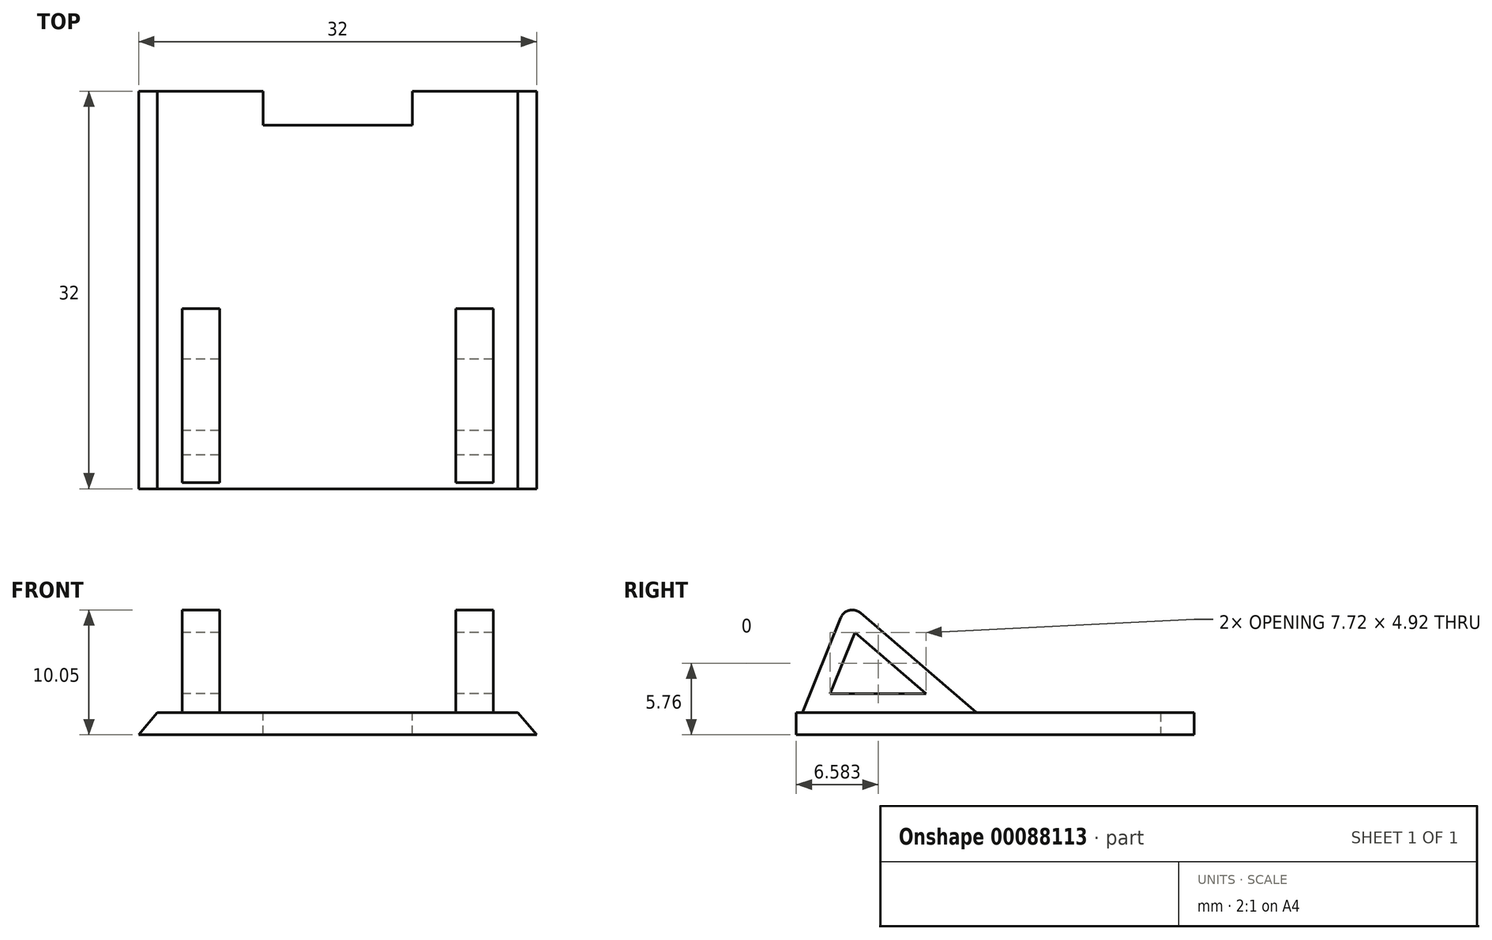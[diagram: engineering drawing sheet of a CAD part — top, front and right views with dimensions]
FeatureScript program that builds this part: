
annotation { "Feature Type Name" : "Feature", "Feature Type Description" : "" }
export const myFeature = defineFeature(function(context is Context, id is Id, definition is map)
    precondition{}
    {
        {
            var Q0;
            Q0=qCreatedBy(makeId("Front.planeOp"),FACE);
            var sketch = newSketch(context, id + "F2", { "sketchPlane" : qUnion([Q0])});
            skLineSegment(sketch, "E0", {"start": v(0, 0) * mm, "end": v(16, 0) * mm});
            skLineSegment(sketch, "E1", {"start": v(0, 0) * mm, "end": v(0, 1.8) * mm});
            skLineSegment(sketch, "E2", {"start": v(0, 1.8) * mm, "end": v(0, 1.8) * mm});
            skLineSegment(sketch, "E3", {"start": v(0, 1.8) * mm, "end": v(14.5, 1.8) * mm});
            skLineSegment(sketch, "E4", {"start": v(16, 0) * mm, "end": v(14.5, 1.8) * mm});
            skLineSegment(sketch, "E5.MirrorCS", {"start": v(0, 1.8) * mm, "end": v(-14.5, 1.8) * mm});
            skLineSegment(sketch, "E6.MirrorCS", {"start": v(0, 0) * mm, "end": v(-16, 0) * mm});
            skLineSegment(sketch, "E7.MirrorCS", {"start": v(-16, 0) * mm, "end": v(-14.5, 1.8) * mm});
            skSolve(sketch);
        }
        {
            var Q0;
            Q0 = qSketchRegion(id + "F2", true);
            extrude(context, id + "F3", {"entities" : qUnion([Q0]), "endBound" : BoundingType.SYMMETRIC, "depth" : 32 * mm});
        }
        {
            var Q0;
            Q0=qCreatedBy(makeId("Top.planeOp"),FACE);
            var sketch = newSketch(context, id + "F4", { "sketchPlane" : qUnion([Q0])});
            skLineSegment(sketch, "E8", {"start": v(0, 0) * mm, "end": v(0, 14.7) * mm, "construction": true});
            skLineSegment(sketch, "E9.bottom", {"start": v(-6, 16.12) * mm, "end": v(6, 16.12) * mm});
            skLineSegment(sketch, "E9.top", {"start": v(-6, 13.28) * mm, "end": v(6, 13.28) * mm});
            skLineSegment(sketch, "E9.left", {"start": v(-6, 16.12) * mm, "end": v(-6, 13.28) * mm});
            skLineSegment(sketch, "E9.right", {"start": v(6, 16.12) * mm, "end": v(6, 13.28) * mm});
            skPoint(sketch, "E9.middle", {"position": v(0, 14.7) * mm});
            skSolve(sketch);
        }
        {
            var Q0;
            Q0 = qSketchRegion(id + "F4", true);
            extrude(context, id + "F5", {"entities" : qUnion([Q0]), "operationType" : NewBodyOperationType.REMOVE, "depth" : 25 * mm});
        }
        {
            var Q0;
            Q0=qCreatedBy(makeId("Right.planeOp"),FACE);
            var sketch = newSketch(context, id + "F0", { "sketchPlane" : qUnion([Q0])});
            skLineSegment(sketch, "E10", {"start": v(0, 0) * mm, "end": v(-15.5, 0) * mm, "construction": true});
            skLineSegment(sketch, "E11", {"start": v(-15.5, 0) * mm, "end": v(-15.5, 1.8) * mm, "construction": true});
            skLineSegment(sketch, "E12", {"start": v(-15.5, 1.8) * mm, "end": v(-15.5, 11.63) * mm});
            skLineSegment(sketch, "E13", {"start": v(-10.85, 9.81) * mm, "end": v(-1.5, 1.8) * mm});
            skLineSegment(sketch, "E14", {"start": v(-1.5, 1.8) * mm, "end": v(-15.5, 1.8) * mm});
            skLineSegment(sketch, "E15", {"start": v(-15.5, 1.8) * mm, "end": v(-12.43, 9.43) * mm});
            skPoint(sketch, "E16.visualSharp", {"position": v(-15.5, 13.8) * mm});
            skArc(sketch, "E16.filletArc", {"start": v(-13.85, 12.39) * mm, "mid": v(-14.92, 12.53) * mm, "end": v(-15.5, 11.63) * mm});
            skArc(sketch, "E17.filletArc", {"start": v(-10.85, 9.81) * mm, "mid": v(-11.74, 10.02) * mm, "end": v(-12.43, 9.43) * mm});
            skLineSegment(sketch, "E18", {"start": v(-13.85, 12.39) * mm, "end": v(-10.85, 9.81) * mm});
            skLineSegment(sketch, "E19.0", {"start": v(-11.3, 8.22) * mm, "end": v(-5.55, 3.3) * mm});
            skLineSegment(sketch, "E19.1", {"start": v(-13.28, 3.3) * mm, "end": v(-11.3, 8.22) * mm});
            skLineSegment(sketch, "E19.2", {"start": v(-5.55, 3.3) * mm, "end": v(-13.28, 3.3) * mm});
            skSolve(sketch);
        }
        {
            var Q0;
            {var subQ0=sQuery(id+"F0.wireOp",EDGE,"E14");Q0=makeQuery(id+"F0.imprint","IMPRINT",FACE,{"disambiguationData":[TD([[makeQuery(id+"F0.imprint","IMPRINT",EDGE,{"derivedFrom":subQ0}),-1.0]])]});}
            extrude(context, id + "F1", {"entities" : qUnion([Q0]), "operationType" : NewBodyOperationType.ADD, "endBound" : BoundingType.SYMMETRIC, "depth" : 25 * mm});
        }
        {
            var Q0;
            {var subQ0=sQuery(id+"F0.wireOp",EDGE,"E14");Q0=makeQuery(id+"F0.imprint","IMPRINT",FACE,{"disambiguationData":[TD([[makeQuery(id+"F0.imprint","IMPRINT",EDGE,{"derivedFrom":subQ0}),-1.0]])]});}
            var Q1;
            {var subQ0=sQuery(id+"F0.wireOp",EDGE,"E12");Q1=makeQuery(id+"F0.imprint","IMPRINT",FACE,{"disambiguationData":[TD([[makeQuery(id+"F0.imprint","IMPRINT",EDGE,{"derivedFrom":subQ0}),-1.0]])]});}
            extrude(context, id + "F6", {"entities" : qUnion([Q0, Q1]), "operationType" : NewBodyOperationType.REMOVE, "endBound" : BoundingType.SYMMETRIC, "depth" : 19 * mm});
        }
    });
